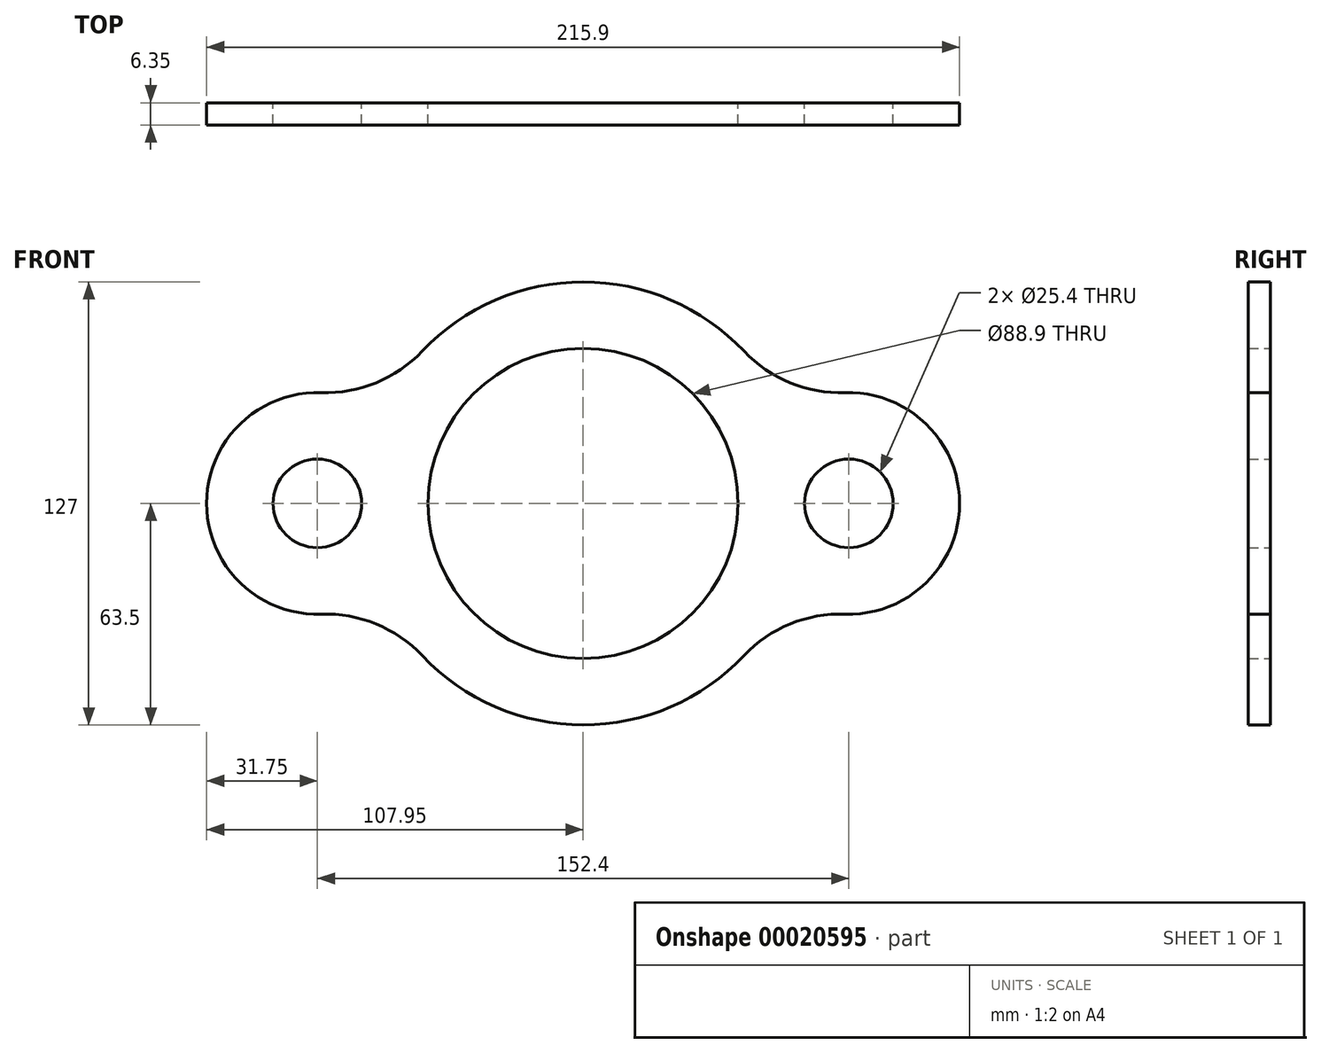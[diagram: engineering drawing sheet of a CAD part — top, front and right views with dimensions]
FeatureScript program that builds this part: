
annotation { "Feature Type Name" : "Feature", "Feature Type Description" : "" }
export const myFeature = defineFeature(function(context is Context, id is Id, definition is map)
    precondition{}
    {
        {
            var Q0;
            Q0=qCreatedBy(makeId("Front.planeOp"),FACE);
            var sketch = newSketch(context, id + "F0", { "sketchPlane" : qUnion([Q0])});
            skCircle(sketch, "E0", {"center": v(0, 0) * mm, "radius": 44.45 * mm});
            skCircle(sketch, "E1", {"center": v(-76.2, 0) * mm, "radius": 12.7 * mm});
            skCircle(sketch, "E2", {"center": v(76.2, 0) * mm, "radius": 12.7 * mm});
            skArc(sketch, "E3", {"start": v(-46.14, -43.63) * mm, "mid": v(0, -63.5) * mm, "end": v(46.14, -43.63) * mm});
            skArc(sketch, "E4", {"start": v(75.12, -31.73) * mm, "mid": v(107.95, 0) * mm, "end": v(75.12, 31.73) * mm});
            skArc(sketch, "E5", {"start": v(-75.12, 31.73) * mm, "mid": v(-107.95, 0) * mm, "end": v(-75.12, -31.73) * mm});
            skArc(sketch, "E6.trimOffspring", {"start": v(46.14, 43.63) * mm, "mid": v(0, 63.5) * mm, "end": v(-46.14, 43.63) * mm});
            skPoint(sketch, "E7.visualSharp", {"position": v(-57.94, 25.98) * mm});
            skArc(sketch, "E7.filletArc", {"start": v(-75.12, 31.73) * mm, "mid": v(-59.35, 34.56) * mm, "end": v(-46.14, 43.63) * mm});
            skPoint(sketch, "E8.visualSharp", {"position": v(-57.94, -25.98) * mm});
            skArc(sketch, "E8.filletArc", {"start": v(-46.14, -43.63) * mm, "mid": v(-59.35, -34.56) * mm, "end": v(-75.12, -31.73) * mm});
            skPoint(sketch, "E9.visualSharp", {"position": v(57.94, -25.98) * mm});
            skArc(sketch, "E9.filletArc", {"start": v(75.12, -31.73) * mm, "mid": v(59.35, -34.56) * mm, "end": v(46.14, -43.63) * mm});
            skPoint(sketch, "E10.visualSharp", {"position": v(57.94, 25.98) * mm});
            skArc(sketch, "E10.filletArc", {"start": v(46.14, 43.63) * mm, "mid": v(59.35, 34.56) * mm, "end": v(75.12, 31.73) * mm});
            skSolve(sketch);
        }
        {
            var Q0;
            Q0=makeQuery(id+"F0.imprint","IMPRINT",FACE,{"disambiguationData":[TD([[makeQuery(id+"F0.imprint","IMPRINT",EDGE,{"derivedFrom":sQuery(id+"F0.wireOp",EDGE,"E0")}),-1.0]])]});
            extrude(context, id + "F1", {"entities" : qUnion([Q0]), "depth" : 6.35 * mm});
        }
    });
